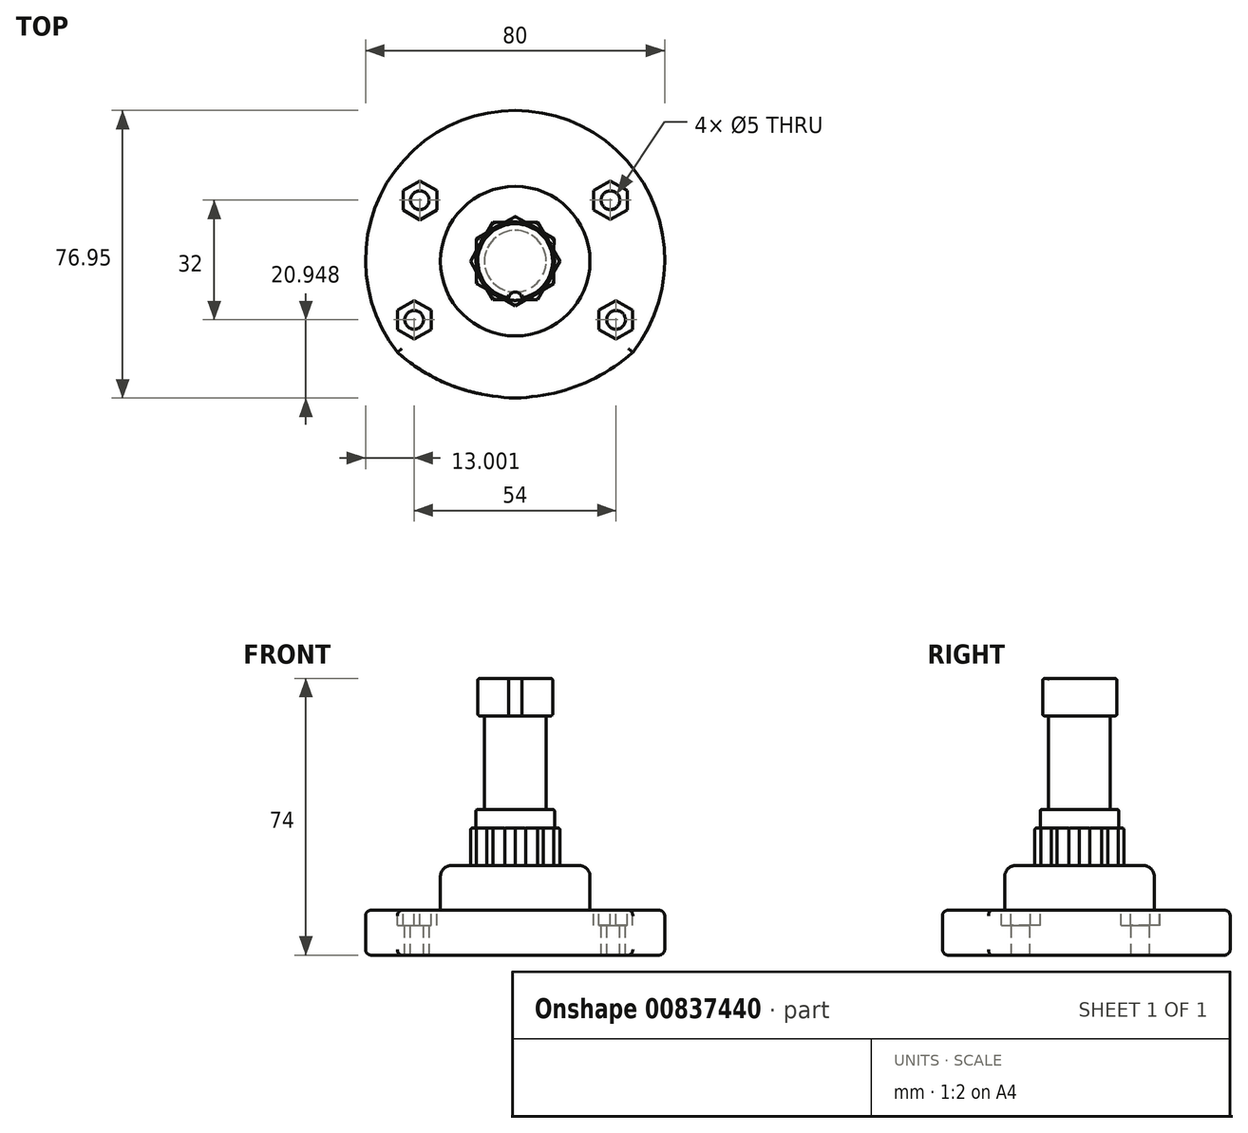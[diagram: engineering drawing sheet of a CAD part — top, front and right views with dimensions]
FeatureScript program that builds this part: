
annotation { "Feature Type Name" : "Feature", "Feature Type Description" : "" }
export const myFeature = defineFeature(function(context is Context, id is Id, definition is map)
    precondition{}
    {
        {
            var Q0;
            Q0=qCreatedBy(makeId("Top.planeOp"),FACE);
            var sketch = newSketch(context, id + "F0", { "sketchPlane" : qUnion([Q0])});
            skCircle(sketch, "E0.cCircle", {"center": v(0, 0) * mm, "radius": 11.95 * mm, "construction": true});
            skLineSegment(sketch, "E0.0", {"start": v(10.36, 5.96) * mm, "end": v(10.36, 2.75) * mm});
            skLineSegment(sketch, "E0.1", {"start": v(10.34, -6) * mm, "end": v(7.56, -7.6) * mm});
            skLineSegment(sketch, "E0.2", {"start": v(-0.02, -11.95) * mm, "end": v(-2.8, -10.34) * mm});
            skLineSegment(sketch, "E0.3", {"start": v(-10.36, -5.96) * mm, "end": v(-10.36, -2.75) * mm});
            skLineSegment(sketch, "E0.4", {"start": v(-10.34, 6) * mm, "end": v(-7.56, 7.6) * mm});
            skLineSegment(sketch, "E0.5", {"start": v(0.02, 11.95) * mm, "end": v(2.8, 10.34) * mm});
            skLineSegment(sketch, "E1", {"start": v(6, 10.34) * mm, "end": v(6.72, 11.59) * mm, "construction": true});
            skLineSegment(sketch, "E2.0", {"start": v(6, 10.34) * mm, "end": v(7.6, 7.56) * mm});
            skLineSegment(sketch, "E2.1", {"start": v(11.95, -0.02) * mm, "end": v(10.34, -2.8) * mm});
            skLineSegment(sketch, "E2.2", {"start": v(5.96, -10.36) * mm, "end": v(2.75, -10.36) * mm});
            skLineSegment(sketch, "E2.3", {"start": v(-6, -10.34) * mm, "end": v(-7.6, -7.56) * mm});
            skLineSegment(sketch, "E2.4", {"start": v(-11.95, 0.02) * mm, "end": v(-10.34, 2.8) * mm});
            skLineSegment(sketch, "E2.5", {"start": v(-5.96, 10.36) * mm, "end": v(-2.75, 10.36) * mm});
            skLineSegment(sketch, "E3.trimOffspring", {"start": v(-7.6, -7.56) * mm, "end": v(-10.36, -5.96) * mm});
            skPoint(sketch, "E4.orphan", {"position": v(-5.2, -8.95) * mm});
            skLineSegment(sketch, "E5.trimOffspring", {"start": v(-10.36, -2.75) * mm, "end": v(-11.95, 0.02) * mm});
            skLineSegment(sketch, "E6.trimOffspring", {"start": v(-2.8, -10.34) * mm, "end": v(-6, -10.34) * mm});
            skLineSegment(sketch, "E7.trimOffspring", {"start": v(2.75, -10.36) * mm, "end": v(-0.02, -11.95) * mm});
            skLineSegment(sketch, "E8.trimOffspring", {"start": v(7.56, -7.6) * mm, "end": v(5.96, -10.36) * mm});
            skLineSegment(sketch, "E9.trimOffspring", {"start": v(-10.34, 2.8) * mm, "end": v(-10.34, 6) * mm});
            skLineSegment(sketch, "E10.trimOffspring", {"start": v(-7.56, 7.6) * mm, "end": v(-5.96, 10.36) * mm});
            skLineSegment(sketch, "E11.trimOffspring", {"start": v(-2.75, 10.36) * mm, "end": v(0.02, 11.95) * mm});
            skLineSegment(sketch, "E12.trimOffspring", {"start": v(2.8, 10.34) * mm, "end": v(6, 10.34) * mm});
            skLineSegment(sketch, "E13.trimOffspring", {"start": v(7.6, 7.56) * mm, "end": v(10.36, 5.96) * mm});
            skPoint(sketch, "E14.orphan", {"position": v(5.2, 8.95) * mm});
            skLineSegment(sketch, "E15.trimOffspring", {"start": v(10.36, 2.75) * mm, "end": v(11.95, -0.02) * mm});
            skLineSegment(sketch, "E16.trimOffspring", {"start": v(10.34, -2.8) * mm, "end": v(10.34, -6) * mm});
            skSolve(sketch);
        }
        {
            var Q0;
            Q0=makeQuery(id+"F0.imprint","IMPRINT",FACE,{"disambiguationData":[TD([[makeQuery(id+"F0.imprint","IMPRINT",EDGE,{"derivedFrom":sQuery(id+"F0.wireOp",EDGE,"E0.0")}),-1.0]])]});
            extrude(context, id + "F1", {"entities" : qUnion([Q0]), "depth" : 10 * mm, "offsetDistance" : 25 * mm});
        }
        {
            var Q0;
            Q0=makeQuery(id+"F1.opExtrude","CAP_FACE",FACE,{"disambiguationData":[OSD([sQuery(id+"F0.wireOp",EDGE,"E0.0"),sQuery(id+"F0.wireOp",EDGE,"E0.1"),sQuery(id+"F0.wireOp",EDGE,"E0.2"),sQuery(id+"F0.wireOp",EDGE,"E0.3"),sQuery(id+"F0.wireOp",EDGE,"E0.4"),sQuery(id+"F0.wireOp",EDGE,"E0.5"),sQuery(id+"F0.wireOp",EDGE,"E2.0"),sQuery(id+"F0.wireOp",EDGE,"E2.1"),sQuery(id+"F0.wireOp",EDGE,"E2.2"),sQuery(id+"F0.wireOp",EDGE,"E2.3"),sQuery(id+"F0.wireOp",EDGE,"E2.4"),sQuery(id+"F0.wireOp",EDGE,"E2.5"),sQuery(id+"F0.wireOp",EDGE,"E3.trimOffspring"),sQuery(id+"F0.wireOp",EDGE,"E5.trimOffspring"),sQuery(id+"F0.wireOp",EDGE,"E6.trimOffspring"),sQuery(id+"F0.wireOp",EDGE,"E7.trimOffspring"),sQuery(id+"F0.wireOp",EDGE,"E8.trimOffspring"),sQuery(id+"F0.wireOp",EDGE,"E9.trimOffspring"),sQuery(id+"F0.wireOp",EDGE,"E10.trimOffspring"),sQuery(id+"F0.wireOp",EDGE,"E11.trimOffspring"),sQuery(id+"F0.wireOp",EDGE,"E12.trimOffspring"),sQuery(id+"F0.wireOp",EDGE,"E13.trimOffspring"),sQuery(id+"F0.wireOp",EDGE,"E15.trimOffspring"),sQuery(id+"F0.wireOp",EDGE,"E16.trimOffspring")])],"isStart":false});
            var sketch = newSketch(context, id + "F2", { "sketchPlane" : qUnion([Q0])});
            skLineSegment(sketch, "E17", {"start": v(-10.36, -2.75) * mm, "end": v(10.36, 2.75) * mm, "construction": true});
            skLineSegment(sketch, "E18", {"start": v(2.75, -10.36) * mm, "end": v(-2.75, 10.36) * mm, "construction": true});
            skCircle(sketch, "E19", {"center": v(0, 0) * mm, "radius": 10.5 * mm});
            skSolve(sketch);
        }
        {
            var Q0;
            Q0=makeQuery(id+"F2.imprint","IMPRINT",FACE,{"disambiguationData":[TD([[makeQuery(id+"F2.imprint","IMPRINT",EDGE,{"derivedFrom":sQuery(id+"F2.wireOp",EDGE,"E19")}),1.0]])]});
            extrude(context, id + "F3", {"entities" : qUnion([Q0]), "operationType" : NewBodyOperationType.ADD, "depth" : 5 * mm, "offsetDistance" : 25 * mm});
        }
        {
            var Q0;
            Q0=makeQuery(id+"F1.opExtrude","CAP_EDGE",EDGE,{"disambiguationData":[OSD([sQuery(id+"F0.wireOp",EDGE,"E2.5")])],"isStart":false});
            var Q1;
            Q1=makeQuery(id+"F1.opExtrude","CAP_EDGE",EDGE,{"disambiguationData":[OSD([sQuery(id+"F0.wireOp",EDGE,"E10.trimOffspring")])],"isStart":false});
            var Q2;
            Q2=makeQuery(id+"F1.opExtrude","CAP_EDGE",EDGE,{"disambiguationData":[OSD([sQuery(id+"F0.wireOp",EDGE,"E0.4")])],"isStart":false});
            var Q3;
            Q3=makeQuery(id+"F1.opExtrude","CAP_EDGE",EDGE,{"disambiguationData":[OSD([sQuery(id+"F0.wireOp",EDGE,"E9.trimOffspring")])],"isStart":false});
            var Q4;
            Q4=makeQuery(id+"F1.opExtrude","CAP_EDGE",EDGE,{"disambiguationData":[OSD([sQuery(id+"F0.wireOp",EDGE,"E2.4")])],"isStart":false});
            var Q5;
            Q5=makeQuery(id+"F1.opExtrude","CAP_EDGE",EDGE,{"disambiguationData":[OSD([sQuery(id+"F0.wireOp",EDGE,"E5.trimOffspring")])],"isStart":false});
            var Q6;
            Q6=makeQuery(id+"F1.opExtrude","CAP_EDGE",EDGE,{"disambiguationData":[OSD([sQuery(id+"F0.wireOp",EDGE,"E0.3")])],"isStart":false});
            var Q7;
            Q7=makeQuery(id+"F1.opExtrude","CAP_EDGE",EDGE,{"disambiguationData":[OSD([sQuery(id+"F0.wireOp",EDGE,"E3.trimOffspring")])],"isStart":false});
            var Q8;
            Q8=makeQuery(id+"F1.opExtrude","CAP_EDGE",EDGE,{"disambiguationData":[OSD([sQuery(id+"F0.wireOp",EDGE,"E2.3")])],"isStart":false});
            var Q9;
            Q9=makeQuery(id+"F1.opExtrude","CAP_EDGE",EDGE,{"disambiguationData":[OSD([sQuery(id+"F0.wireOp",EDGE,"E6.trimOffspring")])],"isStart":false});
            var Q10;
            Q10=makeQuery(id+"F1.opExtrude","CAP_EDGE",EDGE,{"disambiguationData":[OSD([sQuery(id+"F0.wireOp",EDGE,"E0.2")])],"isStart":false});
            var Q11;
            Q11=makeQuery(id+"F1.opExtrude","CAP_EDGE",EDGE,{"disambiguationData":[OSD([sQuery(id+"F0.wireOp",EDGE,"E7.trimOffspring")])],"isStart":false});
            var Q12;
            Q12=makeQuery(id+"F1.opExtrude","CAP_EDGE",EDGE,{"disambiguationData":[OSD([sQuery(id+"F0.wireOp",EDGE,"E2.2")])],"isStart":false});
            var Q13;
            Q13=makeQuery(id+"F1.opExtrude","CAP_EDGE",EDGE,{"disambiguationData":[OSD([sQuery(id+"F0.wireOp",EDGE,"E8.trimOffspring")])],"isStart":false});
            var Q14;
            Q14=makeQuery(id+"F1.opExtrude","CAP_EDGE",EDGE,{"disambiguationData":[OSD([sQuery(id+"F0.wireOp",EDGE,"E0.1")])],"isStart":false});
            var Q15;
            Q15=makeQuery(id+"F1.opExtrude","CAP_EDGE",EDGE,{"disambiguationData":[OSD([sQuery(id+"F0.wireOp",EDGE,"E16.trimOffspring")])],"isStart":false});
            var Q16;
            Q16=makeQuery(id+"F1.opExtrude","CAP_EDGE",EDGE,{"disambiguationData":[OSD([sQuery(id+"F0.wireOp",EDGE,"E2.1")])],"isStart":false});
            var Q17;
            Q17=makeQuery(id+"F1.opExtrude","CAP_EDGE",EDGE,{"disambiguationData":[OSD([sQuery(id+"F0.wireOp",EDGE,"E15.trimOffspring")])],"isStart":false});
            var Q18;
            Q18=makeQuery(id+"F1.opExtrude","CAP_EDGE",EDGE,{"disambiguationData":[OSD([sQuery(id+"F0.wireOp",EDGE,"E0.0")])],"isStart":false});
            var Q19;
            Q19=makeQuery(id+"F1.opExtrude","CAP_EDGE",EDGE,{"disambiguationData":[OSD([sQuery(id+"F0.wireOp",EDGE,"E13.trimOffspring")])],"isStart":false});
            var Q20;
            Q20=makeQuery(id+"F1.opExtrude","CAP_EDGE",EDGE,{"disambiguationData":[OSD([sQuery(id+"F0.wireOp",EDGE,"E2.0")])],"isStart":false});
            var Q21;
            Q21=makeQuery(id+"F1.opExtrude","CAP_EDGE",EDGE,{"disambiguationData":[OSD([sQuery(id+"F0.wireOp",EDGE,"E12.trimOffspring")])],"isStart":false});
            var Q22;
            Q22=makeQuery(id+"F1.opExtrude","CAP_EDGE",EDGE,{"disambiguationData":[OSD([sQuery(id+"F0.wireOp",EDGE,"E0.5")])],"isStart":false});
            var Q23;
            Q23=makeQuery(id+"F1.opExtrude","CAP_EDGE",EDGE,{"disambiguationData":[OSD([sQuery(id+"F0.wireOp",EDGE,"E11.trimOffspring")])],"isStart":false});
            fillet(context, id + "F4", {"entities" : qUnion([Q0, Q1, Q2, Q3, Q4, Q5, Q6, Q7, Q8, Q9, Q10, Q11, Q12, Q13, Q14, Q15, Q16, Q17, Q18, Q19, Q20, Q21, Q22, Q23]), "radius" : .5 * mm, "tangentPropagation" : true, "allowEdgeOverflow" : false});
        }
        {
            var Q0;
            Q0=makeQuery(id+"F3.opExtrude","CAP_FACE",FACE,{"disambiguationData":[OSD([sQuery(id+"F2.wireOp",EDGE,"E19")])],"isStart":false});
            var sketch = newSketch(context, id + "F5", { "sketchPlane" : qUnion([Q0])});
            skCircle(sketch, "E20", {"center": v(0, 0) * mm, "radius": 8.25 * mm});
            skSolve(sketch);
        }
        {
            var Q0;
            Q0=makeQuery(id+"F5.imprint","IMPRINT",FACE,{"disambiguationData":[TD([[makeQuery(id+"F5.imprint","IMPRINT",EDGE,{"derivedFrom":sQuery(id+"F5.wireOp",EDGE,"E20")}),1.0]])]});
            extrude(context, id + "F6", {"entities" : qUnion([Q0]), "operationType" : NewBodyOperationType.ADD, "depth" : 25 * mm, "offsetDistance" : 25 * mm});
        }
        {
            var Q0;
            Q0=makeQuery(id+"F6.opExtrude","CAP_FACE",FACE,{"disambiguationData":[OSD([sQuery(id+"F5.wireOp",EDGE,"E20")])],"isStart":false});
            var sketch = newSketch(context, id + "F7", { "sketchPlane" : qUnion([Q0])});
            skCircle(sketch, "E21", {"center": v(0, 0) * mm, "radius": 10 * mm});
            skSolve(sketch);
        }
        {
            var Q0;
            Q0=makeQuery(id+"F7.imprint","IMPRINT",FACE,{"disambiguationData":[TD([[makeQuery(id+"F7.imprint","IMPRINT",EDGE,{"derivedFrom":sQuery(id+"F7.wireOp",EDGE,"E21")}),1.0]])]});
            var Q1;
            Q1=makeQuery(id+"F7.imprint","IMPRINT",FACE,{"disambiguationData":[TD([[makeQuery(id+"F7.imprint","IMPRINT",EDGE,{"derivedFrom":makeQuery(id+"F6.opExtrude","CAP_EDGE",EDGE,{"disambiguationData":[OSD([sQuery(id+"F5.wireOp",EDGE,"E20")])],"isStart":false})}),1.0]])]});
            extrude(context, id + "F8", {"entities" : qUnion([Q0, Q1]), "operationType" : NewBodyOperationType.ADD, "depth" : 10 * mm, "offsetDistance" : 25 * mm});
        }
        {
            var Q0;
            Q0=makeQuery(id+"F8.opExtrude","CAP_FACE",FACE,{"disambiguationData":[OSD([sQuery(id+"F7.wireOp",EDGE,"E21")])],"isStart":true});
            var sketch = newSketch(context, id + "F9", { "sketchPlane" : qUnion([Q0])});
            skLineSegment(sketch, "E22", {"start": v(0, 10) * mm, "end": v(0, 8.25) * mm, "construction": true});
            skArc(sketch, "E23", {"start": v(0, 8.25) * mm, "mid": v(1.18, 8.7) * mm, "end": v(1.74, 9.85) * mm});
            skArc(sketch, "E24", {"start": v(0, 8.25) * mm, "mid": v(-1.18, 8.7) * mm, "end": v(-1.74, 9.85) * mm});
            skSolve(sketch);
        }
        {
            var Q0;
            {var subQ0=sQuery(id+"F9.wireOp",EDGE,"E23");Q0=makeQuery(id+"F9.imprint","IMPRINT",FACE,{"disambiguationData":[TD([[makeQuery(id+"F9.imprint","IMPRINT",EDGE,{"derivedFrom":subQ0}),1.0]])]});}
            extrude(context, id + "F10", {"entities" : qUnion([Q0]), "operationType" : NewBodyOperationType.REMOVE, "oppositeDirection" : true, "depth" : 25 * mm, "offsetDistance" : 25 * mm});
        }
        {
            var Q0;
            Q0=makeQuery(id+"F8.opExtrude","CAP_EDGE",EDGE,{"disambiguationData":[OSD([sQuery(id+"F7.wireOp",EDGE,"E21")])],"isStart":false});
            var Q1;
            Q1=makeQuery(id+"F10.boolean.opBoolean","INTERSECT",EDGE,{"derivedFrom":[makeQuery(id+"F8.opExtrude","CAP_FACE",FACE,{"disambiguationData":[OSD([sQuery(id+"F7.wireOp",EDGE,"E21")])],"isStart":false}),makeQuery(id+"F10.opExtrude","SWEPT_FACE",FACE,{"disambiguationData":[OSD([sQuery(id+"F9.wireOp",EDGE,"E23"),sQuery(id+"F9.wireOp",EDGE,"E24")])]})]});
            var Q2;
            Q2=makeQuery(id+"F10.boolean.opBoolean","COPY",EDGE,{"derivedFrom":makeQuery(id+"F10.opExtrude","SWEPT_EDGE",EDGE,{"disambiguationData":[OSD([sQuery(id+"F7.wireOp",EDGE,"E21"),sQuery(id+"F9.wireOp",EDGE,"E24")])]})});
            var Q3;
            Q3=makeQuery(id+"F10.boolean.opBoolean","COPY",EDGE,{"derivedFrom":makeQuery(id+"F10.opExtrude","SWEPT_EDGE",EDGE,{"disambiguationData":[OSD([sQuery(id+"F7.wireOp",EDGE,"E21"),sQuery(id+"F9.wireOp",EDGE,"E23")])]})});
            var Q4;
            Q4=makeQuery(id+"F8.opExtrude","CAP_EDGE",EDGE,{"disambiguationData":[OSD([sQuery(id+"F7.wireOp",EDGE,"E21")])],"isStart":true});
            var Q5;
            Q5=makeQuery(id+"F10.boolean.opBoolean","COPY",EDGE,{"disambiguationData":[OD(1.0)],"derivedFrom":makeQuery(id+"F10.opExtrude","CAP_EDGE",EDGE,{"disambiguationData":[OSD([sQuery(id+"F9.wireOp",EDGE,"E23"),sQuery(id+"F9.wireOp",EDGE,"E24")])],"isStart":true})});
            var Q6;
            Q6=makeQuery(id+"F10.boolean.opBoolean","COPY",EDGE,{"disambiguationData":[OD(0.0)],"derivedFrom":makeQuery(id+"F10.opExtrude","CAP_EDGE",EDGE,{"disambiguationData":[OSD([sQuery(id+"F9.wireOp",EDGE,"E23"),sQuery(id+"F9.wireOp",EDGE,"E24")])],"isStart":true})});
            fillet(context, id + "F11", {"entities" : qUnion([Q0, Q1, Q2, Q3, Q4, Q5, Q6]), "radius" : .5 * mm, "tangentPropagation" : true, "allowEdgeOverflow" : false});
        }
        {
            var Q0;
            Q0=makeQuery(id+"F6.opExtrude","CAP_EDGE",EDGE,{"disambiguationData":[OSD([sQuery(id+"F5.wireOp",EDGE,"E20")])],"isStart":true});
            var Q1;
            Q1=makeQuery(id+"F3.opExtrude","CAP_EDGE",EDGE,{"disambiguationData":[OSD([sQuery(id+"F2.wireOp",EDGE,"E19")])],"isStart":false});
            fillet(context, id + "F12", {"entities" : qUnion([Q0, Q1]), "radius" : .5 * mm, "tangentPropagation" : true, "allowEdgeOverflow" : false});
        }
        {
            var Q0;
            Q0=makeQuery(id+"F1.opExtrude","CAP_FACE",FACE,{"disambiguationData":[OSD([sQuery(id+"F0.wireOp",EDGE,"E0.0"),sQuery(id+"F0.wireOp",EDGE,"E0.1"),sQuery(id+"F0.wireOp",EDGE,"E0.2"),sQuery(id+"F0.wireOp",EDGE,"E0.3"),sQuery(id+"F0.wireOp",EDGE,"E0.4"),sQuery(id+"F0.wireOp",EDGE,"E0.5"),sQuery(id+"F0.wireOp",EDGE,"E2.0"),sQuery(id+"F0.wireOp",EDGE,"E2.1"),sQuery(id+"F0.wireOp",EDGE,"E2.2"),sQuery(id+"F0.wireOp",EDGE,"E2.3"),sQuery(id+"F0.wireOp",EDGE,"E2.4"),sQuery(id+"F0.wireOp",EDGE,"E2.5"),sQuery(id+"F0.wireOp",EDGE,"E3.trimOffspring"),sQuery(id+"F0.wireOp",EDGE,"E5.trimOffspring"),sQuery(id+"F0.wireOp",EDGE,"E6.trimOffspring"),sQuery(id+"F0.wireOp",EDGE,"E7.trimOffspring"),sQuery(id+"F0.wireOp",EDGE,"E8.trimOffspring"),sQuery(id+"F0.wireOp",EDGE,"E9.trimOffspring"),sQuery(id+"F0.wireOp",EDGE,"E10.trimOffspring"),sQuery(id+"F0.wireOp",EDGE,"E11.trimOffspring"),sQuery(id+"F0.wireOp",EDGE,"E12.trimOffspring"),sQuery(id+"F0.wireOp",EDGE,"E13.trimOffspring"),sQuery(id+"F0.wireOp",EDGE,"E15.trimOffspring"),sQuery(id+"F0.wireOp",EDGE,"E16.trimOffspring")])],"isStart":true});
            var sketch = newSketch(context, id + "F13", { "sketchPlane" : qUnion([Q0])});
            skCircle(sketch, "E25", {"center": v(0, 0) * mm, "radius": 20 * mm});
            skSolve(sketch);
        }
        {
            var Q0;
            Q0=makeQuery(id+"F13.imprint","IMPRINT",FACE,{"disambiguationData":[TD([[makeQuery(id+"F13.imprint","IMPRINT",EDGE,{"derivedFrom":sQuery(id+"F13.wireOp",EDGE,"E25")}),1.0]])]});
            var Q1;
            Q1=makeQuery(id+"F13.imprint","IMPRINT",FACE,{"disambiguationData":[TD([[makeQuery(id+"F13.imprint","IMPRINT",EDGE,{"derivedFrom":makeQuery(id+"F1.opExtrude","CAP_EDGE",EDGE,{"disambiguationData":[OSD([sQuery(id+"F0.wireOp",EDGE,"E0.0")])],"isStart":true})}),1.0]])]});
            extrude(context, id + "F14", {"entities" : qUnion([Q0, Q1]), "operationType" : NewBodyOperationType.ADD, "depth" : 12 * mm, "offsetDistance" : 25 * mm});
        }
        {
            var Q0;
            Q0=makeQuery(id+"F14.opExtrude","CAP_EDGE",EDGE,{"disambiguationData":[OSD([sQuery(id+"F13.wireOp",EDGE,"E25")])],"isStart":true});
            fillet(context, id + "F15", {"entities" : qUnion([Q0]), "radius" : 3 * mm, "tangentPropagation" : true, "allowEdgeOverflow" : false});
        }
        {
            var Q0;
            Q0=makeQuery(id+"F14.opExtrude","CAP_FACE",FACE,{"disambiguationData":[OSD([sQuery(id+"F13.wireOp",EDGE,"E25")])],"isStart":false});
            var sketch = newSketch(context, id + "F16", { "sketchPlane" : qUnion([Q0])});
            skPoint(sketch, "E26.middle", {"position": v(-0.03, -0.3) * mm});
            skPoint(sketch, "E27.start.orphan", {"position": v(-0.03, -40.3) * mm});
            skPoint(sketch, "E28.visualSharp", {"position": v(34.22, 20.36) * mm});
            skPoint(sketch, "E29.visualSharp", {"position": v(-34.6, 19.81) * mm});
            skPoint(sketch, "E30.start.orphan", {"position": v(26.97, -16.3) * mm});
            skPoint(sketch, "E31.start.orphan", {"position": v(-27.03, -16.3) * mm});
            skCircle(sketch, "E32", {"center": v(25.47, -16.3) * mm, "radius": 2.5 * mm});
            skCircle(sketch, "E33", {"center": v(-25.53, -16.3) * mm, "radius": 2.5 * mm});
            skPoint(sketch, "E34.center.orphan", {"position": v(26.97, 15.7) * mm});
            skCircle(sketch, "E35", {"center": v(26.97, 15.7) * mm, "radius": 2.5 * mm});
            skCircle(sketch, "E36", {"center": v(-27.03, 15.7) * mm, "radius": 2.5 * mm});
            skArc(sketch, "E37", {"start": v(-34.6, 19.81) * mm, "mid": v(0.29, -40.3) * mm, "end": v(34.22, 20.36) * mm});
            skPoint(sketch, "E38.endSnap0", {"position": v(-0.03, 24.47) * mm});
            skPoint(sketch, "E39.orphan", {"position": v(-0.03, 39.7) * mm});
            skPoint(sketch, "E40.visualSharp", {"position": v(31.38, 24.47) * mm});
            skPoint(sketch, "E41.visualSharp", {"position": v(-31.43, 24.47) * mm});
            skLineSegment(sketch, "E42", {"start": v(-0.03, -0.3) * mm, "end": v(-0.03, 39.7) * mm});
            skArc(sketch, "E43", {"start": v(-31.43, 24.47) * mm, "mid": v(-0.03, -40.3) * mm, "end": v(31.38, 24.47) * mm});
            skFitSpline(sketch, "E44", {"points": [v(-31.43, 24.47) * mm, v(-0.03, 36.64) * mm, v(31.38, 24.47) * mm], "startDerivative": vector(50.74, 44.21) * mm, "endDerivative": vector(11.96, -59.12) * mm});
            skFitSpline(sketch, "E45.MirrorCS", {"points": [v(31.38, 24.47) * mm, v(-0.03, 36.64) * mm, v(-31.43, 24.47) * mm], "startDerivative": vector(-50.74, 44.21) * mm, "endDerivative": vector(-11.96, -59.12) * mm});
            skSolve(sketch);
        }
        {
            var Q0;
            Q0=makeQuery(id+"F16.imprint","IMPRINT",FACE,{"disambiguationData":[TD([[makeQuery(id+"F16.imprint","IMPRINT",EDGE,{"derivedFrom":sQuery(id+"F16.wireOp",EDGE,"E32")}),-1.0]])]});
            var Q1;
            Q1=makeQuery(id+"F16.imprint","IMPRINT",FACE,{"disambiguationData":[TD([[makeQuery(id+"F16.imprint","IMPRINT",EDGE,{"derivedFrom":makeQuery(id+"F14.opExtrude","CAP_EDGE",EDGE,{"disambiguationData":[OSD([sQuery(id+"F13.wireOp",EDGE,"E25")])],"isStart":false})}),1.0]])]});
            extrude(context, id + "F17", {"entities" : qUnion([Q0, Q1]), "operationType" : NewBodyOperationType.ADD, "depth" : 12 * mm, "offsetDistance" : 25 * mm});
        }
        {
            var Q0;
            Q0=makeQuery(id+"F17.opExtrude","CAP_EDGE",EDGE,{"disambiguationData":[OSD([sQuery(id+"F16.wireOp",EDGE,"E37")])],"isStart":true});
            var Q1;
            Q1=makeQuery(id+"F17.opExtrude","CAP_EDGE",EDGE,{"disambiguationData":[OSD([sQuery(id+"F16.wireOp",EDGE,"E37")])],"isStart":false});
            var Q2;
            Q2=makeQuery(id+"F14.opExtrude","CAP_EDGE",EDGE,{"disambiguationData":[OSD([sQuery(id+"F13.wireOp",EDGE,"E25")])],"isStart":false});
            fillet(context, id + "F18", {"entities" : qUnion([Q0, Q1, Q2]), "radius" : 1.5 * mm, "tangentPropagation" : true, "allowEdgeOverflow" : false});
        }
        {
            var Q0;
            Q0=makeQuery(id+"F17.opExtrude","CAP_EDGE",EDGE,{"disambiguationData":[OSD([sQuery(id+"F16.wireOp",EDGE,"E43")])],"isStart":true});
            var Q1;
            Q1=makeQuery(id+"F17.opExtrude","CAP_EDGE",EDGE,{"disambiguationData":[OSD([sQuery(id+"F16.wireOp",EDGE,"E43")])],"isStart":false});
            var Q2;
            Q2=makeQuery(id+"F17.opExtrude","CAP_EDGE",EDGE,{"disambiguationData":[OSD([sQuery(id+"F16.wireOp",EDGE,"E44")])],"isStart":true});
            var Q3;
            Q3=makeQuery(id+"F17.opExtrude","CAP_EDGE",EDGE,{"disambiguationData":[OSD([sQuery(id+"F16.wireOp",EDGE,"E45.MirrorCS")])],"isStart":true});
            var Q4;
            Q4=makeQuery(id+"F17.opExtrude","CAP_EDGE",EDGE,{"disambiguationData":[OSD([sQuery(id+"F16.wireOp",EDGE,"E44")])],"isStart":false});
            var Q5;
            Q5=makeQuery(id+"F17.opExtrude","CAP_EDGE",EDGE,{"disambiguationData":[OSD([sQuery(id+"F16.wireOp",EDGE,"E45.MirrorCS")])],"isStart":false});
            var Q6;
            Q6=makeQuery(id+"F17.opExtrude","SWEPT_EDGE",EDGE,{"disambiguationData":[OSD([sQuery(id+"F16.wireOp",EDGE,"E43"),sQuery(id+"F16.wireOp",EDGE,"E44")])]});
            var Q7;
            Q7=makeQuery(id+"F17.opExtrude","SWEPT_EDGE",EDGE,{"disambiguationData":[OSD([sQuery(id+"F16.wireOp",EDGE,"E44"),sQuery(id+"F16.wireOp",EDGE,"E45.MirrorCS")])]});
            var Q8;
            Q8=makeQuery(id+"F17.opExtrude","SWEPT_EDGE",EDGE,{"disambiguationData":[OSD([sQuery(id+"F16.wireOp",EDGE,"E43"),sQuery(id+"F16.wireOp",EDGE,"E45.MirrorCS")])]});
            fillet(context, id + "F19", {"entities" : qUnion([Q0, Q1, Q2, Q3, Q4, Q5, Q6, Q7, Q8]), "radius" : 1.5 * mm, "tangentPropagation" : true, "allowEdgeOverflow" : false});
        }
        {
            var Q0;
            Q0=makeQuery(id+"F17.opExtrude","CAP_FACE",FACE,{"disambiguationData":[OSD([sQuery(id+"F16.wireOp",EDGE,"E32"),sQuery(id+"F16.wireOp",EDGE,"E33"),sQuery(id+"F16.wireOp",EDGE,"E35"),sQuery(id+"F16.wireOp",EDGE,"E36"),sQuery(id+"F16.wireOp",EDGE,"E43"),sQuery(id+"F16.wireOp",EDGE,"E44"),sQuery(id+"F16.wireOp",EDGE,"E45.MirrorCS")])],"isStart":true});
            var sketch = newSketch(context, id + "F20", { "sketchPlane" : qUnion([Q0])});
            skLineSegment(sketch, "E46", {"start": v(-25.48, 18.8) * mm, "end": v(-25.48, 13.8) * mm});
            skLineSegment(sketch, "E47", {"start": v(-28.03, 16.29) * mm, "end": v(-23.03, 16.29) * mm});
            skCircle(sketch, "E48.cCircle", {"center": v(-25.48, 16.29) * mm, "radius": 4.5 * mm, "construction": true});
            skLineSegment(sketch, "E48.0", {"start": v(-20.98, 18.89) * mm, "end": v(-20.98, 13.7) * mm});
            skLineSegment(sketch, "E48.1", {"start": v(-20.98, 13.7) * mm, "end": v(-25.48, 11.1) * mm});
            skLineSegment(sketch, "E48.2", {"start": v(-25.48, 11.1) * mm, "end": v(-29.98, 13.7) * mm});
            skLineSegment(sketch, "E48.3", {"start": v(-29.98, 13.7) * mm, "end": v(-29.98, 18.89) * mm});
            skLineSegment(sketch, "E48.4", {"start": v(-29.98, 18.89) * mm, "end": v(-25.48, 21.49) * mm});
            skLineSegment(sketch, "E48.5", {"start": v(-25.48, 21.49) * mm, "end": v(-20.98, 18.89) * mm});
            skPoint(sketch, "E48.0.midPoint", {"position": v(-20.98, 16.29) * mm});
            skLineSegment(sketch, "E49", {"start": v(22.97, 16.34) * mm, "end": v(27.97, 16.34) * mm});
            skLineSegment(sketch, "E50", {"start": v(25.47, 16.3) * mm, "end": v(25.47, 18.8) * mm});
            skLineSegment(sketch, "E51", {"start": v(25.47, 18.8) * mm, "end": v(25.47, 13.8) * mm});
            skCircle(sketch, "E52.cCircle", {"center": v(25.47, 16.3) * mm, "radius": 4.5 * mm, "construction": true});
            skLineSegment(sketch, "E52.0", {"start": v(20.97, 13.7) * mm, "end": v(20.97, 18.9) * mm});
            skLineSegment(sketch, "E52.1", {"start": v(20.97, 18.9) * mm, "end": v(25.47, 21.5) * mm});
            skLineSegment(sketch, "E52.2", {"start": v(25.47, 21.5) * mm, "end": v(29.97, 18.9) * mm});
            skLineSegment(sketch, "E52.3", {"start": v(29.97, 18.9) * mm, "end": v(29.97, 13.7) * mm});
            skLineSegment(sketch, "E52.4", {"start": v(29.97, 13.7) * mm, "end": v(25.47, 11.11) * mm});
            skLineSegment(sketch, "E52.5", {"start": v(25.47, 11.11) * mm, "end": v(20.97, 13.7) * mm});
            skPoint(sketch, "E52.0.midPoint", {"position": v(20.97, 16.3) * mm});
            skLineSegment(sketch, "E53", {"start": v(-26.98, -13.2) * mm, "end": v(-26.98, -18.2) * mm});
            skLineSegment(sketch, "E54", {"start": v(-26.98, -15.7) * mm, "end": v(-24.53, -15.7) * mm});
            skLineSegment(sketch, "E55", {"start": v(-24.53, -15.7) * mm, "end": v(-29.53, -15.7) * mm});
            skCircle(sketch, "E56.cCircle", {"center": v(-26.98, -15.7) * mm, "radius": 4.5 * mm, "construction": true});
            skLineSegment(sketch, "E56.0", {"start": v(-22.48, -13.1) * mm, "end": v(-22.48, -18.3) * mm});
            skLineSegment(sketch, "E56.1", {"start": v(-22.48, -18.3) * mm, "end": v(-26.98, -20.89) * mm});
            skLineSegment(sketch, "E56.2", {"start": v(-26.98, -20.89) * mm, "end": v(-31.48, -18.3) * mm});
            skLineSegment(sketch, "E56.3", {"start": v(-31.48, -18.3) * mm, "end": v(-31.48, -13.1) * mm});
            skLineSegment(sketch, "E56.4", {"start": v(-31.48, -13.1) * mm, "end": v(-26.98, -10.5) * mm});
            skLineSegment(sketch, "E56.5", {"start": v(-26.98, -10.5) * mm, "end": v(-22.48, -13.1) * mm});
            skPoint(sketch, "E56.0.midPoint", {"position": v(-22.48, -15.7) * mm});
            skLineSegment(sketch, "E57", {"start": v(26.9, -13.2) * mm, "end": v(26.9, -18.2) * mm});
            skLineSegment(sketch, "E58", {"start": v(26.97, -15.7) * mm, "end": v(24.47, -15.7) * mm});
            skPoint(sketch, "E58.endSnap0", {"position": v(26.9, -15.7) * mm});
            skLineSegment(sketch, "E59", {"start": v(24.47, -15.7) * mm, "end": v(29.47, -15.7) * mm});
            skCircle(sketch, "E60.cCircle", {"center": v(26.9, -15.7) * mm, "radius": 4.5 * mm, "construction": true});
            skLineSegment(sketch, "E60.0", {"start": v(31.4, -13.1) * mm, "end": v(31.4, -18.3) * mm});
            skLineSegment(sketch, "E60.1", {"start": v(31.4, -18.3) * mm, "end": v(26.9, -20.89) * mm});
            skLineSegment(sketch, "E60.2", {"start": v(26.9, -20.89) * mm, "end": v(22.4, -18.3) * mm});
            skLineSegment(sketch, "E60.3", {"start": v(22.4, -18.3) * mm, "end": v(22.4, -13.1) * mm});
            skLineSegment(sketch, "E60.4", {"start": v(22.4, -13.1) * mm, "end": v(26.9, -10.5) * mm});
            skLineSegment(sketch, "E60.5", {"start": v(26.9, -10.5) * mm, "end": v(31.4, -13.1) * mm});
            skPoint(sketch, "E60.0.midPoint", {"position": v(31.4, -15.7) * mm});
            skSolve(sketch);
        }
        {
            var Q0;
            Q0=makeQuery(id+"F20.imprint","IMPRINT",FACE,{"disambiguationData":[TD([[makeQuery(id+"F20.imprint","IMPRINT",EDGE,{"derivedFrom":sQuery(id+"F20.wireOp",EDGE,"E48.0")}),-1.0]])]});
            var Q1;
            Q1=makeQuery(id+"F20.imprint","IMPRINT",FACE,{"disambiguationData":[TD([[makeQuery(id+"F20.imprint","IMPRINT",EDGE,{"derivedFrom":sQuery(id+"F20.wireOp",EDGE,"E52.0")}),-1.0]])]});
            var Q2;
            Q2=makeQuery(id+"F20.imprint","IMPRINT",FACE,{"disambiguationData":[TD([[makeQuery(id+"F20.imprint","IMPRINT",EDGE,{"derivedFrom":sQuery(id+"F20.wireOp",EDGE,"E60.0")}),-1.0]])]});
            var Q3;
            Q3=makeQuery(id+"F20.imprint","IMPRINT",FACE,{"disambiguationData":[TD([[makeQuery(id+"F20.imprint","IMPRINT",EDGE,{"derivedFrom":sQuery(id+"F20.wireOp",EDGE,"E56.0")}),-1.0]])]});
            extrude(context, id + "F21", {"entities" : qUnion([Q0, Q1, Q2, Q3]), "operationType" : NewBodyOperationType.REMOVE, "oppositeDirection" : true, "depth" : 4 * mm, "offsetDistance" : 25 * mm});
        }
    });
